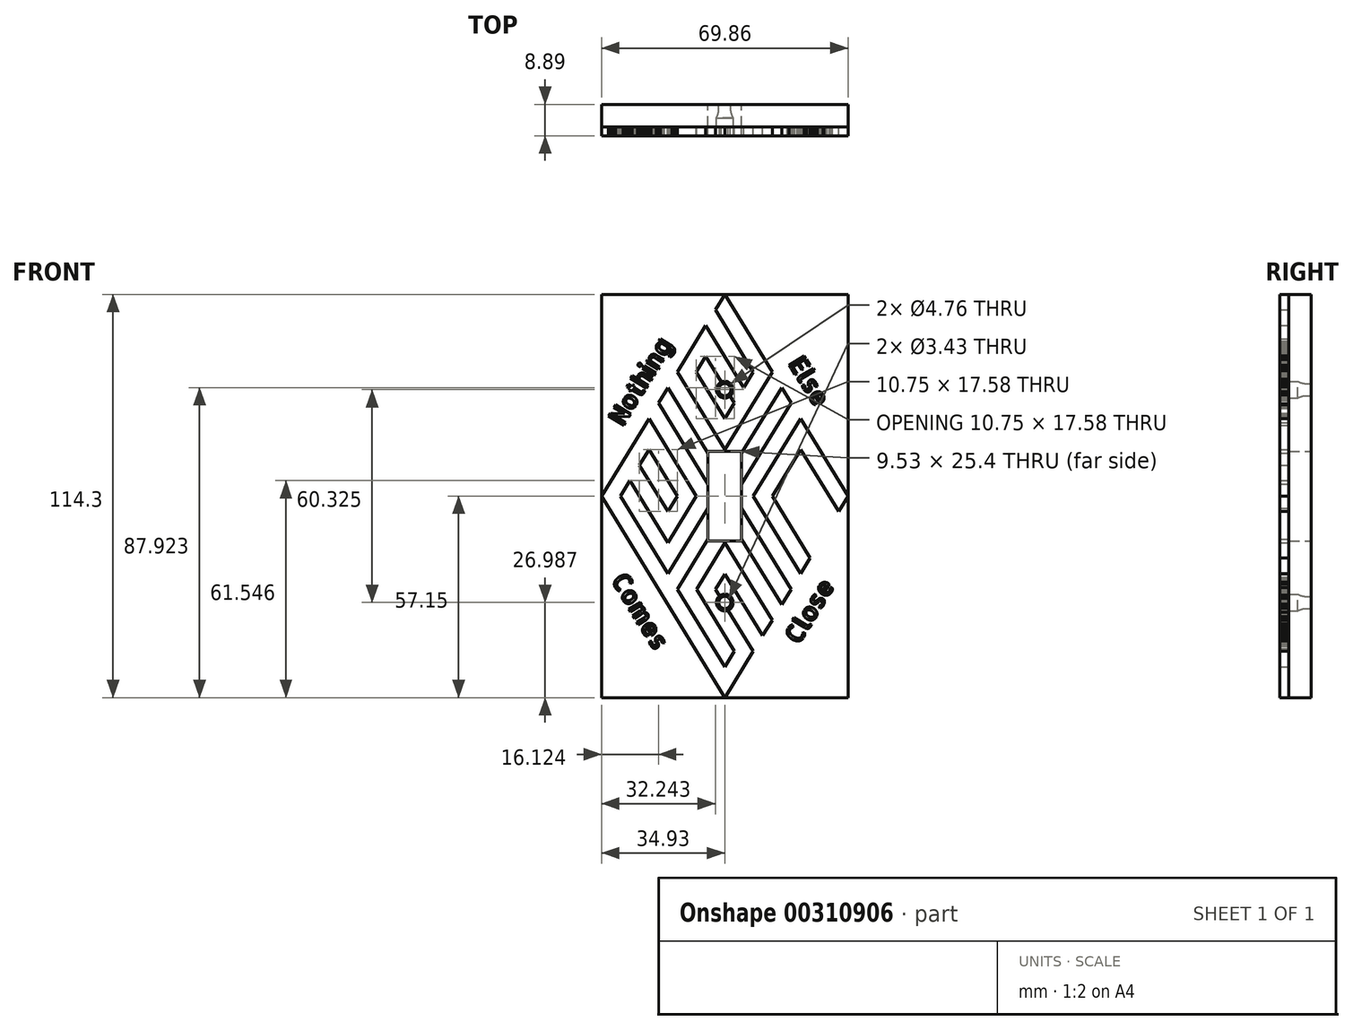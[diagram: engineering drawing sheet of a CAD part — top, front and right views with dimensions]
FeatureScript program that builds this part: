
annotation { "Feature Type Name" : "Feature", "Feature Type Description" : "" }
export const myFeature = defineFeature(function(context is Context, id is Id, definition is map)
    precondition{}
    {
        {
            var Q0;
            Q0=qCreatedBy(makeId("Front.planeOp"),FACE);
            var sketch = newSketch(context, id + "F0", { "sketchPlane" : qUnion([Q0])});
            skLineSegment(sketch, "E0.bottom", {"start": v(34.92, 57.15) * mm, "end": v(-34.93, 57.15) * mm});
            skLineSegment(sketch, "E0.top", {"start": v(34.93, -57.15) * mm, "end": v(-34.92, -57.15) * mm});
            skLineSegment(sketch, "E0.left", {"start": v(34.92, 57.15) * mm, "end": v(34.93, -57.15) * mm});
            skLineSegment(sketch, "E0.right", {"start": v(-34.93, 57.15) * mm, "end": v(-34.92, -57.15) * mm});
            skPoint(sketch, "E0.middle", {"position": v(0, 0) * mm});
            skLineSegment(sketch, "E1.bottom", {"start": v(4.76, 12.7) * mm, "end": v(-4.76, 12.7) * mm});
            skLineSegment(sketch, "E1.top", {"start": v(4.76, -12.7) * mm, "end": v(-4.76, -12.7) * mm});
            skLineSegment(sketch, "E1.left", {"start": v(4.76, 12.7) * mm, "end": v(4.76, -12.7) * mm});
            skLineSegment(sketch, "E1.right", {"start": v(-4.76, 12.7) * mm, "end": v(-4.76, -12.7) * mm});
            skCircle(sketch, "E2", {"center": v(0, 30.16) * mm, "radius": 2.38 * mm});
            skCircle(sketch, "E3", {"center": v(0, -30.16) * mm, "radius": 2.38 * mm});
            skSolve(sketch);
        }
        {
            var Q0;
            Q0 = qSketchRegion(id + "F0", true);
            extrude(context, id + "F1", {"entities" : qUnion([Q0]), "depth" : 6.35 * mm});
        }
        {
            var Q0;
            Q0=makeQuery(id+"F1.opExtrude","CAP_FACE",FACE,{"disambiguationData":[OSD([sQuery(id+"F0.wireOp",EDGE,"E0.bottom"),sQuery(id+"F0.wireOp",EDGE,"E0.top"),sQuery(id+"F0.wireOp",EDGE,"E0.left"),sQuery(id+"F0.wireOp",EDGE,"E0.right"),sQuery(id+"F0.wireOp",EDGE,"E1.bottom"),sQuery(id+"F0.wireOp",EDGE,"E1.top"),sQuery(id+"F0.wireOp",EDGE,"E1.left"),sQuery(id+"F0.wireOp",EDGE,"E1.right"),sQuery(id+"F0.wireOp",EDGE,"E2"),sQuery(id+"F0.wireOp",EDGE,"E3")])],"isStart":false});
            var sketch = newSketch(context, id + "F2", { "sketchPlane" : qUnion([Q0])});
            skLineSegment(sketch, "E4", {"start": v(0, -57.15) * mm, "end": v(-34.92, 0) * mm});
            skLineSegment(sketch, "E5", {"start": v(-26.87, 4.4) * mm, "end": v(-29.55, 0) * mm});
            skPoint(sketch, "E6.endSnap0", {"position": v(-17.46, -28.58) * mm});
            skLineSegment(sketch, "E7", {"start": v(-13.43, -26.38) * mm, "end": v(0, -48.36) * mm});
            skLineSegment(sketch, "E8", {"start": v(0.06, -13.29) * mm, "end": v(13.43, -35.17) * mm});
            skLineSegment(sketch, "E9", {"start": v(13.43, -35.17) * mm, "end": v(10.75, -39.57) * mm});
            skLineSegment(sketch, "E10", {"start": v(-18.8, 26.38) * mm, "end": v(-4.76, 3.4) * mm});
            skLineSegment(sketch, "E11", {"start": v(16.12, -30.77) * mm, "end": v(18.8, -26.38) * mm});
            skLineSegment(sketch, "E12", {"start": v(18.8, -26.38) * mm, "end": v(4.76, -3.4) * mm});
            skLineSegment(sketch, "E13", {"start": v(-16.12, 30.77) * mm, "end": v(-18.8, 26.38) * mm});
            skLineSegment(sketch, "E14", {"start": v(-16.12, -13.19) * mm, "end": v(-8.06, 0) * mm});
            skLineSegment(sketch, "E15", {"start": v(-16.12, -21.98) * mm, "end": v(-29.55, 0) * mm});
            skLineSegment(sketch, "E16", {"start": v(-24.18, 8.8) * mm, "end": v(-16.12, -4.4) * mm});
            skLineSegment(sketch, "E17", {"start": v(-24.18, 8.8) * mm, "end": v(-21.5, 13.19) * mm});
            skLineSegment(sketch, "E18", {"start": v(-16.12, -4.4) * mm, "end": v(-13.43, 0) * mm});
            skLineSegment(sketch, "E19", {"start": v(-13.43, 0) * mm, "end": v(-21.5, 13.19) * mm});
            skLineSegment(sketch, "E20", {"start": v(-16.12, -21.98) * mm, "end": v(-4.76, -3.4) * mm});
            skLineSegment(sketch, "E21", {"start": v(-8.06, 0) * mm, "end": v(-21.5, 21.98) * mm});
            skLineSegment(sketch, "E22", {"start": v(-13.43, -26.38) * mm, "end": v(-4.76, -12.19) * mm});
            skLineSegment(sketch, "E23", {"start": v(-26.87, 4.4) * mm, "end": v(-16.12, -13.19) * mm});
            skLineSegment(sketch, "E24", {"start": v(13.43, 35.17) * mm, "end": v(0, 13.19) * mm});
            skLineSegment(sketch, "E25", {"start": v(0, 13.19) * mm, "end": v(-13.43, 35.17) * mm});
            skLineSegment(sketch, "E26", {"start": v(-2.69, 52.75) * mm, "end": v(8.06, 35.17) * mm});
            skLineSegment(sketch, "E27", {"start": v(8.06, 35.17) * mm, "end": v(5.37, 30.77) * mm});
            skLineSegment(sketch, "E28", {"start": v(5.37, 30.77) * mm, "end": v(-5.37, 48.36) * mm});
            skLineSegment(sketch, "E29", {"start": v(-5.37, 39.57) * mm, "end": v(-8.06, 35.17) * mm});
            skLineSegment(sketch, "E30", {"start": v(-5.37, 39.57) * mm, "end": v(-0.96, 32.34) * mm});
            skLineSegment(sketch, "E31", {"start": v(2.69, 26.38) * mm, "end": v(0, 21.98) * mm});
            skLineSegment(sketch, "E32", {"start": v(0, 21.98) * mm, "end": v(-8.06, 35.17) * mm});
            skLineSegment(sketch, "E33", {"start": v(21.5, 21.98) * mm, "end": v(34.92, 0) * mm});
            skLineSegment(sketch, "E34", {"start": v(34.93, 0) * mm, "end": v(32.24, -4.4) * mm});
            skLineSegment(sketch, "E35", {"start": v(13.43, 0) * mm, "end": v(24.18, -17.58) * mm});
            skLineSegment(sketch, "E36", {"start": v(24.18, -17.58) * mm, "end": v(21.5, -21.98) * mm});
            skLineSegment(sketch, "E37", {"start": v(8.06, 0) * mm, "end": v(21.5, 21.98) * mm});
            skLineSegment(sketch, "E38", {"start": v(32.24, -4.4) * mm, "end": v(21.5, 13.19) * mm});
            skLineSegment(sketch, "E39", {"start": v(21.5, -21.98) * mm, "end": v(8.06, 0) * mm});
            skLineSegment(sketch, "E40", {"start": v(0, -48.36) * mm, "end": v(2.69, -43.96) * mm});
            skLineSegment(sketch, "E41", {"start": v(0.06, -13.29) * mm, "end": v(-8, -26.48) * mm});
            skLineSegment(sketch, "E42", {"start": v(2.69, -43.96) * mm, "end": v(-8, -26.48) * mm});
            skLineSegment(sketch, "E43", {"start": v(10.75, -39.57) * mm, "end": v(0.06, -22.08) * mm});
            skLineSegment(sketch, "E44", {"start": v(0.06, -22.08) * mm, "end": v(-2.63, -26.48) * mm});
            skLineSegment(sketch, "E45", {"start": v(-2.63, -26.48) * mm, "end": v(-1.5, -28.31) * mm});
            skLineSegment(sketch, "E46", {"start": v(-2.69, 52.75) * mm, "end": v(0, 57.15) * mm});
            skLineSegment(sketch, "E47", {"start": v(0, 57.15) * mm, "end": v(13.43, 35.17) * mm});
            skLineSegment(sketch, "E48", {"start": v(-5.37, 48.36) * mm, "end": v(-13.43, 35.17) * mm});
            skLineSegment(sketch, "E49.trimOffspring", {"start": v(4.76, 12.19) * mm, "end": v(16.12, 30.77) * mm});
            skLineSegment(sketch, "E50.trimOffspring", {"start": v(4.76, -12.19) * mm, "end": v(16.12, -30.77) * mm});
            skLineSegment(sketch, "E51.trimOffspring", {"start": v(-4.76, 12.19) * mm, "end": v(-16.12, 30.77) * mm});
            skLineSegment(sketch, "E52.trimOffspring", {"start": v(4.76, 3.4) * mm, "end": v(18.8, 26.38) * mm});
            skLineSegment(sketch, "E53", {"start": v(18.8, 26.38) * mm, "end": v(16.12, 30.77) * mm});
            skLineSegment(sketch, "E54", {"start": v(13.43, 0) * mm, "end": v(21.5, 13.19) * mm});
            skLineSegment(sketch, "E55", {"start": v(8.06, -43.96) * mm, "end": v(0, -57.15) * mm});
            skLineSegment(sketch, "E56", {"start": v(-21.5, 21.98) * mm, "end": v(-34.92, 0) * mm});
            skLineSegment(sketch, "E57.0", {"start": v(4.76, 12.7) * mm, "end": v(4.76, -12.7) * mm});
            skLineSegment(sketch, "E58.0", {"start": v(4.76, 12.7) * mm, "end": v(-4.76, 12.7) * mm});
            skLineSegment(sketch, "E59.0", {"start": v(-4.76, 12.7) * mm, "end": v(-4.76, -12.7) * mm});
            skLineSegment(sketch, "E60.0", {"start": v(4.76, -12.7) * mm, "end": v(-4.76, -12.7) * mm});
            skArc(sketch, "E61.0", {"start": v(-0.96, 32.34) * mm, "mid": v(-2.03, 28.92) * mm, "end": v(1.5, 28.31) * mm});
            skArc(sketch, "E62.0", {"start": v(-1.5, -28.31) * mm, "mid": v(-2.03, -31.4) * mm, "end": v(0.96, -32.34) * mm});
            skLineSegment(sketch, "E63.trimOffspring", {"start": v(0.96, -32.34) * mm, "end": v(8.06, -43.96) * mm});
            skLineSegment(sketch, "E64.trimOffspring", {"start": v(1.5, 28.31) * mm, "end": v(2.69, 26.38) * mm});
            skSolve(sketch);
        }
        {
            var Q0;
            Q0=makeQuery(id+"F2.imprint","IMPRINT",FACE,{"disambiguationData":[TD([[makeQuery(id+"F2.imprint","IMPRINT",EDGE,{"derivedFrom":sQuery(id+"F2.wireOp",EDGE,"E24")}),-1.0]])]});
            var Q1;
            {var subQ0=sQuery(id+"F2.wireOp",EDGE,"E10");Q1=makeQuery(id+"F2.imprint","IMPRINT",FACE,{"disambiguationData":[TD([[makeQuery(id+"F2.imprint","IMPRINT",EDGE,{"derivedFrom":subQ0}),1.0]])]});}
            var Q2;
            Q2=makeQuery(id+"F2.imprint","IMPRINT",FACE,{"disambiguationData":[TD([[makeQuery(id+"F2.imprint","IMPRINT",EDGE,{"derivedFrom":sQuery(id+"F2.wireOp",EDGE,"E4")}),-1.0]])]});
            var Q3;
            Q3=makeQuery(id+"F2.imprint","IMPRINT",FACE,{"disambiguationData":[TD([[makeQuery(id+"F2.imprint","IMPRINT",EDGE,{"derivedFrom":sQuery(id+"F2.wireOp",EDGE,"E11")}),1.0]])]});
            var Q4;
            Q4=makeQuery(id+"F2.imprint","IMPRINT",FACE,{"disambiguationData":[TD([[makeQuery(id+"F2.imprint","IMPRINT",EDGE,{"derivedFrom":sQuery(id+"F2.wireOp",EDGE,"E33")}),-1.0]])]});
            var Q5;
            {var subQ0=sQuery(id+"F2.wireOp",EDGE,"E49.trimOffspring");Q5=makeQuery(id+"F2.imprint","IMPRINT",FACE,{"disambiguationData":[TD([[makeQuery(id+"F2.imprint","IMPRINT",EDGE,{"derivedFrom":subQ0}),-1.0]])]});}
            extrude(context, id + "F3", {"entities" : qUnion([Q0, Q1, Q2, Q3, Q4, Q5]), "depth" : 2.54 * mm});
        }
        {
            var Q0;
            {var subQ0=sQuery(id+"F0.wireOp",EDGE,"E1.right");var subQ1=sQuery(id+"F0.wireOp",EDGE,"E1.left");var subQ2=sQuery(id+"F0.wireOp",EDGE,"E1.top");var subQ3=sQuery(id+"F0.wireOp",EDGE,"E1.bottom");var subQ4=sQuery(id+"F0.wireOp",EDGE,"E0.right");var subQ5=sQuery(id+"F0.wireOp",EDGE,"E3");var subQ6=sQuery(id+"F2.wireOp",EDGE,"E10");var subQ7=sQuery(id+"F0.wireOp",EDGE,"E0.bottom");var subQ8=sQuery(id+"F0.wireOp",EDGE,"E0.left");var subQ9=sQuery(id+"F0.wireOp",EDGE,"E0.top");var subQ10=makeQuery(id+"F1.opExtrude","CAP_FACE",FACE,{"disambiguationData":[OSD([subQ7,subQ9,subQ8,subQ4,subQ3,subQ2,subQ1,subQ0,sQuery(id+"F0.wireOp",EDGE,"E2"),subQ5])],"isStart":false});var subQ11=sQuery(id+"F2.wireOp",EDGE,"E20");var subQ12=sQuery(id+"F2.wireOp",EDGE,"E22");var subQ13=sQuery(id+"F2.wireOp",EDGE,"E12");var subQ14=sQuery(id+"F2.wireOp",EDGE,"E49.trimOffspring");var subQ15=sQuery(id+"F2.wireOp",EDGE,"E50.trimOffspring");var subQ16=sQuery(id+"F2.wireOp",EDGE,"E51.trimOffspring");var subQ17=sQuery(id+"F2.wireOp",EDGE,"E52.trimOffspring");var subQ18=sQuery(id+"F2.wireOp",EDGE,"E57.0");var subQ19=sQuery(id+"F2.wireOp",EDGE,"E59.0");Q0=makeQuery(id+"F3.boolean.opBoolean","SPLIT",FACE,{"disambiguationData":[TD([makeQuery(id+"F1.opExtrude","SWEPT_FACE",FACE,{"disambiguationData":[OSD([subQ7])]}),subQ10,makeQuery(id+"F1.opExtrude","SWEPT_FACE",FACE,{"disambiguationData":[OSD([subQ9])]}),makeQuery(id+"F1.opExtrude","SWEPT_FACE",FACE,{"disambiguationData":[OSD([subQ8])]}),makeQuery(id+"F1.opExtrude","SWEPT_FACE",FACE,{"disambiguationData":[OSD([subQ4])]}),makeQuery(id+"F1.opExtrude","SWEPT_FACE",FACE,{"disambiguationData":[OSD([subQ3])]}),makeQuery(id+"F1.opExtrude","SWEPT_FACE",FACE,{"disambiguationData":[OSD([subQ2])]}),makeQuery(id+"F1.opExtrude","SWEPT_FACE",FACE,{"disambiguationData":[OSD([subQ1])]}),makeQuery(id+"F1.opExtrude","SWEPT_FACE",FACE,{"disambiguationData":[OSD([subQ0])]}),makeQuery(id+"F1.opExtrude","SWEPT_FACE",FACE,{"disambiguationData":[OSD([subQ5])]}),makeQuery(id+"F3.opExtrude","SWEPT_FACE",FACE,{"disambiguationData":[OSD([sQuery(id+"F2.wireOp",EDGE,"E4")])]}),makeQuery(id+"F3.opExtrude","SWEPT_FACE",FACE,{"disambiguationData":[OSD([sQuery(id+"F2.wireOp",EDGE,"E5")])]}),makeQuery(id+"F3.opExtrude","SWEPT_FACE",FACE,{"disambiguationData":[OSD([sQuery(id+"F2.wireOp",EDGE,"E7")])]}),makeQuery(id+"F3.opExtrude","SWEPT_FACE",FACE,{"disambiguationData":[OSD([sQuery(id+"F2.wireOp",EDGE,"E8")])]}),makeQuery(id+"F3.opExtrude","SWEPT_FACE",FACE,{"disambiguationData":[OSD([sQuery(id+"F2.wireOp",EDGE,"E9")])]}),makeQuery(id+"F3.opExtrude","SWEPT_FACE",FACE,{"disambiguationData":[OSD([subQ6])]}),makeQuery(id+"F3.opExtrude","SWEPT_FACE",FACE,{"disambiguationData":[OSD([sQuery(id+"F2.wireOp",EDGE,"E11")])]}),makeQuery(id+"F3.opExtrude","SWEPT_FACE",FACE,{"disambiguationData":[OSD([subQ13])]}),makeQuery(id+"F3.opExtrude","SWEPT_FACE",FACE,{"disambiguationData":[OSD([sQuery(id+"F2.wireOp",EDGE,"E13")])]}),makeQuery(id+"F3.opExtrude","SWEPT_FACE",FACE,{"disambiguationData":[OSD([sQuery(id+"F2.wireOp",EDGE,"E14")])]}),makeQuery(id+"F3.opExtrude","SWEPT_FACE",FACE,{"disambiguationData":[OSD([sQuery(id+"F2.wireOp",EDGE,"E15")])]}),makeQuery(id+"F3.opExtrude","SWEPT_FACE",FACE,{"disambiguationData":[OSD([subQ11])]}),makeQuery(id+"F3.opExtrude","SWEPT_FACE",FACE,{"disambiguationData":[OSD([sQuery(id+"F2.wireOp",EDGE,"E21")])]}),makeQuery(id+"F3.opExtrude","SWEPT_FACE",FACE,{"disambiguationData":[OSD([subQ12])]}),makeQuery(id+"F3.opExtrude","SWEPT_FACE",FACE,{"disambiguationData":[OSD([sQuery(id+"F2.wireOp",EDGE,"E23")])]}),makeQuery(id+"F3.opExtrude","SWEPT_FACE",FACE,{"disambiguationData":[OSD([sQuery(id+"F2.wireOp",EDGE,"E24")])]}),makeQuery(id+"F3.opExtrude","SWEPT_FACE",FACE,{"disambiguationData":[OSD([sQuery(id+"F2.wireOp",EDGE,"E25")])]}),makeQuery(id+"F3.opExtrude","SWEPT_FACE",FACE,{"disambiguationData":[OSD([sQuery(id+"F2.wireOp",EDGE,"E26")])]}),makeQuery(id+"F3.opExtrude","SWEPT_FACE",FACE,{"disambiguationData":[OSD([sQuery(id+"F2.wireOp",EDGE,"E27")])]}),makeQuery(id+"F3.opExtrude","SWEPT_FACE",FACE,{"disambiguationData":[OSD([sQuery(id+"F2.wireOp",EDGE,"E28")])]}),makeQuery(id+"F3.opExtrude","SWEPT_FACE",FACE,{"disambiguationData":[OSD([sQuery(id+"F2.wireOp",EDGE,"E33")])]}),makeQuery(id+"F3.opExtrude","SWEPT_FACE",FACE,{"disambiguationData":[OSD([sQuery(id+"F2.wireOp",EDGE,"E34")])]}),makeQuery(id+"F3.opExtrude","SWEPT_FACE",FACE,{"disambiguationData":[OSD([sQuery(id+"F2.wireOp",EDGE,"E35")])]}),makeQuery(id+"F3.opExtrude","SWEPT_FACE",FACE,{"disambiguationData":[OSD([sQuery(id+"F2.wireOp",EDGE,"E36")])]}),makeQuery(id+"F3.opExtrude","SWEPT_FACE",FACE,{"disambiguationData":[OSD([sQuery(id+"F2.wireOp",EDGE,"E37")])]}),makeQuery(id+"F3.opExtrude","SWEPT_FACE",FACE,{"disambiguationData":[OSD([sQuery(id+"F2.wireOp",EDGE,"E38")])]}),makeQuery(id+"F3.opExtrude","SWEPT_FACE",FACE,{"disambiguationData":[OSD([sQuery(id+"F2.wireOp",EDGE,"E39")])]}),makeQuery(id+"F3.opExtrude","SWEPT_FACE",FACE,{"disambiguationData":[OSD([sQuery(id+"F2.wireOp",EDGE,"E40")])]}),makeQuery(id+"F3.opExtrude","SWEPT_FACE",FACE,{"disambiguationData":[OSD([sQuery(id+"F2.wireOp",EDGE,"E41")])]}),makeQuery(id+"F3.opExtrude","SWEPT_FACE",FACE,{"disambiguationData":[OSD([sQuery(id+"F2.wireOp",EDGE,"E42")])]}),makeQuery(id+"F3.opExtrude","SWEPT_FACE",FACE,{"disambiguationData":[OSD([sQuery(id+"F2.wireOp",EDGE,"E43")])]}),makeQuery(id+"F3.opExtrude","SWEPT_FACE",FACE,{"disambiguationData":[OSD([sQuery(id+"F2.wireOp",EDGE,"E44")])]}),makeQuery(id+"F3.opExtrude","SWEPT_FACE",FACE,{"disambiguationData":[OSD([sQuery(id+"F2.wireOp",EDGE,"E45")])]}),makeQuery(id+"F3.opExtrude","SWEPT_FACE",FACE,{"disambiguationData":[OSD([sQuery(id+"F2.wireOp",EDGE,"E46")])]}),makeQuery(id+"F3.opExtrude","SWEPT_FACE",FACE,{"disambiguationData":[OSD([sQuery(id+"F2.wireOp",EDGE,"E47")])]}),makeQuery(id+"F3.opExtrude","SWEPT_FACE",FACE,{"disambiguationData":[OSD([sQuery(id+"F2.wireOp",EDGE,"E48")])]}),makeQuery(id+"F3.opExtrude","SWEPT_FACE",FACE,{"disambiguationData":[OSD([subQ14])]}),makeQuery(id+"F3.opExtrude","SWEPT_FACE",FACE,{"disambiguationData":[OSD([subQ15])]}),makeQuery(id+"F3.opExtrude","SWEPT_FACE",FACE,{"disambiguationData":[OSD([subQ16])]}),makeQuery(id+"F3.opExtrude","SWEPT_FACE",FACE,{"disambiguationData":[OSD([subQ17])]}),makeQuery(id+"F3.opExtrude","SWEPT_FACE",FACE,{"disambiguationData":[OSD([sQuery(id+"F2.wireOp",EDGE,"E53")])]}),makeQuery(id+"F3.opExtrude","SWEPT_FACE",FACE,{"disambiguationData":[OSD([sQuery(id+"F2.wireOp",EDGE,"E54")])]}),makeQuery(id+"F3.opExtrude","SWEPT_FACE",FACE,{"disambiguationData":[OSD([sQuery(id+"F2.wireOp",EDGE,"E55")])]}),makeQuery(id+"F3.opExtrude","SWEPT_FACE",FACE,{"disambiguationData":[OSD([sQuery(id+"F2.wireOp",EDGE,"E56")])]}),makeQuery(id+"F3.opExtrude","SWEPT_FACE",FACE,{"disambiguationData":[OSD([subQ18]),TDD([makeQuery(id+"F2.imprint","IMPRINT",EDGE,{"disambiguationData":[TD([[makeQuery(id+"F2.imprint","INTERSECT",VERTEX,{"derivedFrom":[subQ14,subQ18]}),-1.0]])],"derivedFrom":subQ18})])]}),makeQuery(id+"F3.opExtrude","SWEPT_FACE",FACE,{"disambiguationData":[OSD([subQ18]),TDD([makeQuery(id+"F2.imprint","IMPRINT",EDGE,{"disambiguationData":[TD([[makeQuery(id+"F2.imprint","INTERSECT",VERTEX,{"derivedFrom":[subQ13,subQ18]}),-1.0]])],"derivedFrom":subQ18})])]}),makeQuery(id+"F3.opExtrude","SWEPT_FACE",FACE,{"disambiguationData":[OSD([subQ19]),TDD([makeQuery(id+"F2.imprint","IMPRINT",EDGE,{"disambiguationData":[TD([[makeQuery(id+"F2.imprint","INTERSECT",VERTEX,{"derivedFrom":[subQ6,subQ19]}),1.0]])],"derivedFrom":subQ19})])]}),makeQuery(id+"F3.opExtrude","SWEPT_FACE",FACE,{"disambiguationData":[OSD([subQ19]),TDD([makeQuery(id+"F2.imprint","IMPRINT",EDGE,{"disambiguationData":[TD([[makeQuery(id+"F2.imprint","INTERSECT",VERTEX,{"derivedFrom":[subQ11,subQ19]}),-1.0]])],"derivedFrom":subQ19})])]}),makeQuery(id+"F3.opExtrude","SWEPT_FACE",FACE,{"disambiguationData":[OSD([sQuery(id+"F2.wireOp",EDGE,"E62.0")])]}),makeQuery(id+"F3.opExtrude","SWEPT_FACE",FACE,{"disambiguationData":[OSD([sQuery(id+"F2.wireOp",EDGE,"E63.trimOffspring")])]})])],"derivedFrom":subQ10});}
            var sketch = newSketch(context, id + "F4", { "sketchPlane" : qUnion([Q0])});
            skText(sketch, "E65", { "text": "Else", "fontName": "AllertaStencil-Regular.ttf"});
            skText(sketch, "E66", { "text": "Comes", "fontName": "AllertaStencil-Regular.ttf"});
            skText(sketch, "E67", { "text": "Close", "fontName": "AllertaStencil-Regular.ttf"});
            skText(sketch, "E68", { "text": "Nothing", "fontName": "AllertaStencil-Regular.ttf"});
            skArc(sketch, "E69.0.21", {"start": v(0.96, -32.34) * mm, "mid": v(-2.03, -31.4) * mm, "end": v(-1.5, -28.31) * mm});
            skPoint(sketch, "E70.0.7.end.orphan", {"position": v(-2.69, 52.75) * mm});
            skPoint(sketch, "E71.0.3.end.orphan", {"position": v(4.76, 12.19) * mm});
            skPoint(sketch, "E71.0.2.end.orphan", {"position": v(16.12, 30.77) * mm});
            skPoint(sketch, "E71.0.2.start.orphan", {"position": v(18.8, 26.38) * mm});
            skPoint(sketch, "E69.0.15.end.orphan", {"position": v(-8.06, 0) * mm});
            skPoint(sketch, "E69.0.15.start.orphan", {"position": v(-16.12, -13.19) * mm});
            skPoint(sketch, "E69.0.10.end.orphan", {"position": v(-4.76, -3.4) * mm});
            skPoint(sketch, "E69.0.6.end.orphan", {"position": v(2.69, -43.96) * mm});
            skPoint(sketch, "E69.0.5.end.orphan", {"position": v(-8, -26.48) * mm});
            skPoint(sketch, "E69.0.20.start.orphan", {"position": v(8.06, -43.96) * mm});
            skPoint(sketch, "E69.0.2.end.orphan", {"position": v(10.75, -39.57) * mm});
            skPoint(sketch, "E69.0.1.end.orphan", {"position": v(0.06, -22.08) * mm});
            skPoint(sketch, "E69.0.1.start.orphan", {"position": v(-2.63, -26.48) * mm});
            skPoint(sketch, "E69.0.12.start.orphan", {"position": v(-16.12, -21.98) * mm});
            skPoint(sketch, "E69.0.18.end.orphan", {"position": v(0, -57.15) * mm});
            skPoint(sketch, "E69.0.8.start.orphan", {"position": v(0, -48.36) * mm});
            skPoint(sketch, "E69.0.9.end.orphan", {"position": v(-4.76, -12.19) * mm});
            skPoint(sketch, "E69.0.9.start.orphan", {"position": v(-13.43, -26.38) * mm});
            skPoint(sketch, "E69.0.13.end.orphan", {"position": v(-26.87, 4.4) * mm});
            skPoint(sketch, "E69.0.13.start.orphan", {"position": v(-29.55, 0) * mm});
            skPoint(sketch, "E69.0.17.end.orphan", {"position": v(-34.92, 0) * mm});
            skPoint(sketch, "E69.0.17.start.orphan", {"position": v(-21.5, 21.98) * mm});
            skPoint(sketch, "E72.0.2.end.orphan", {"position": v(-18.8, 26.38) * mm});
            skPoint(sketch, "E72.0.2.start.orphan", {"position": v(-16.12, 30.77) * mm});
            skPoint(sketch, "E72.0.0.end.orphan", {"position": v(-4.76, 12.19) * mm});
            skPoint(sketch, "E72.0.0.start.orphan", {"position": v(-4.76, 3.4) * mm});
            skPoint(sketch, "E73.0.1.end.orphan", {"position": v(16.12, -30.77) * mm});
            skPoint(sketch, "E74.0.3.start.orphan", {"position": v(18.8, -26.38) * mm});
            skPoint(sketch, "E69.0.4.end.orphan", {"position": v(0.06, -13.29) * mm});
            skPoint(sketch, "E69.0.4.start.orphan", {"position": v(13.43, -35.17) * mm});
            skPoint(sketch, "E75.0.5.end.orphan", {"position": v(21.5, 21.98) * mm});
            skPoint(sketch, "E75.0.5.start.orphan", {"position": v(34.92, 0) * mm});
            skPoint(sketch, "E75.0.3.end.orphan", {"position": v(32.24, -4.4) * mm});
            skPoint(sketch, "E75.0.3.start.orphan", {"position": v(21.5, 13.19) * mm});
            skPoint(sketch, "E76.0.0.end.orphan", {"position": v(4.76, -12.19) * mm});
            skPoint(sketch, "E76.0.0.start.orphan", {"position": v(4.76, -3.4) * mm});
            skPoint(sketch, "E70.0.1.end.orphan", {"position": v(5.37, 30.77) * mm});
            skPoint(sketch, "E70.0.1.start.orphan", {"position": v(8.06, 35.17) * mm});
            skPoint(sketch, "E70.0.4.end.orphan", {"position": v(0, 13.19) * mm});
            skPoint(sketch, "E70.0.6.end.orphan", {"position": v(0, 57.15) * mm});
            skPoint(sketch, "E70.0.6.start.orphan", {"position": v(13.43, 35.17) * mm});
            skPoint(sketch, "E70.0.3.end.orphan", {"position": v(-13.43, 35.17) * mm});
            skPoint(sketch, "E70.0.3.start.orphan", {"position": v(-5.37, 48.36) * mm});
            const initialGuessF4  = {"E65": [0.01788, 0.03763, 0.52145, -0.85328, 0.00508], "E66": [-0.03233, -0.02374, 0.52145, -0.85328, 0.00508], "E67": [0.02095, -0.04235, 0.52145, 0.85328, 0.00508], "E68": [-0.02893, 0.01955, 0.52145, 0.85328, 0.00508]};
            skSetInitialGuess(sketch, initialGuessF4);
            skSolve(sketch);
        }
        {
            var Q0;
            Q0 = qSketchRegion(id + "F4", true);
            extrude(context, id + "F5", {"entities" : qUnion([Q0]), "depth" : 2.54 * mm});
        }
        {
            var Q0;
            Q0=makeQuery(id+"F0.imprint","IMPRINT",FACE,{"disambiguationData":[TD([[makeQuery(id+"F0.imprint","IMPRINT",EDGE,{"derivedFrom":sQuery(id+"F0.wireOp",EDGE,"E0.bottom")}),1.0]])]});
            var sketch = newSketch(context, id + "F6", { "sketchPlane" : qUnion([Q0])});
            skCircle(sketch, "E77", {"center": v(0, 30.16) * mm, "radius": 1.71 * mm});
            skCircle(sketch, "E78", {"center": v(0, -30.16) * mm, "radius": 1.71 * mm});
            skLineSegment(sketch, "E79.0.0", {"start": v(-34.92, -57.15) * mm, "end": v(34.93, -57.15) * mm});
            skLineSegment(sketch, "E79.0.1", {"start": v(34.93, -57.15) * mm, "end": v(34.92, 57.15) * mm});
            skLineSegment(sketch, "E79.0.2", {"start": v(34.92, 57.15) * mm, "end": v(-34.93, 57.15) * mm});
            skLineSegment(sketch, "E79.0.3", {"start": v(-34.93, 57.15) * mm, "end": v(-34.92, -57.15) * mm});
            skLineSegment(sketch, "E80.0.0", {"start": v(-4.76, -12.7) * mm, "end": v(4.76, -12.7) * mm});
            skLineSegment(sketch, "E80.0.1", {"start": v(4.76, -12.7) * mm, "end": v(4.76, 12.7) * mm});
            skLineSegment(sketch, "E80.0.2", {"start": v(4.76, 12.7) * mm, "end": v(-4.76, 12.7) * mm});
            skLineSegment(sketch, "E80.0.3", {"start": v(-4.76, 12.7) * mm, "end": v(-4.76, -12.7) * mm});
            skSolve(sketch);
        }
        {
            var Q0;
            Q0 = qSketchRegion(id + "F6", true);
            extrude(context, id + "F7", {"entities" : qUnion([Q0]), "operationType" : NewBodyOperationType.ADD, "depth" : 3.8 * mm});
        }
        {
            var Q0;
            Q0=makeQuery(id+"F7.opExtrude","CAP_EDGE",EDGE,{"disambiguationData":[OSD([sQuery(id+"F6.wireOp",EDGE,"E77")])],"isStart":false});
            var Q1;
            Q1=makeQuery(id+"F7.opExtrude","CAP_EDGE",EDGE,{"disambiguationData":[OSD([sQuery(id+"F6.wireOp",EDGE,"E78")])],"isStart":false});
            fillet(context, id + "F8", {"entities" : qUnion([Q0, Q1]), "radius" : 4.76 * mm, "tangentPropagation" : true, "allowEdgeOverflow" : false});
        }
    });
